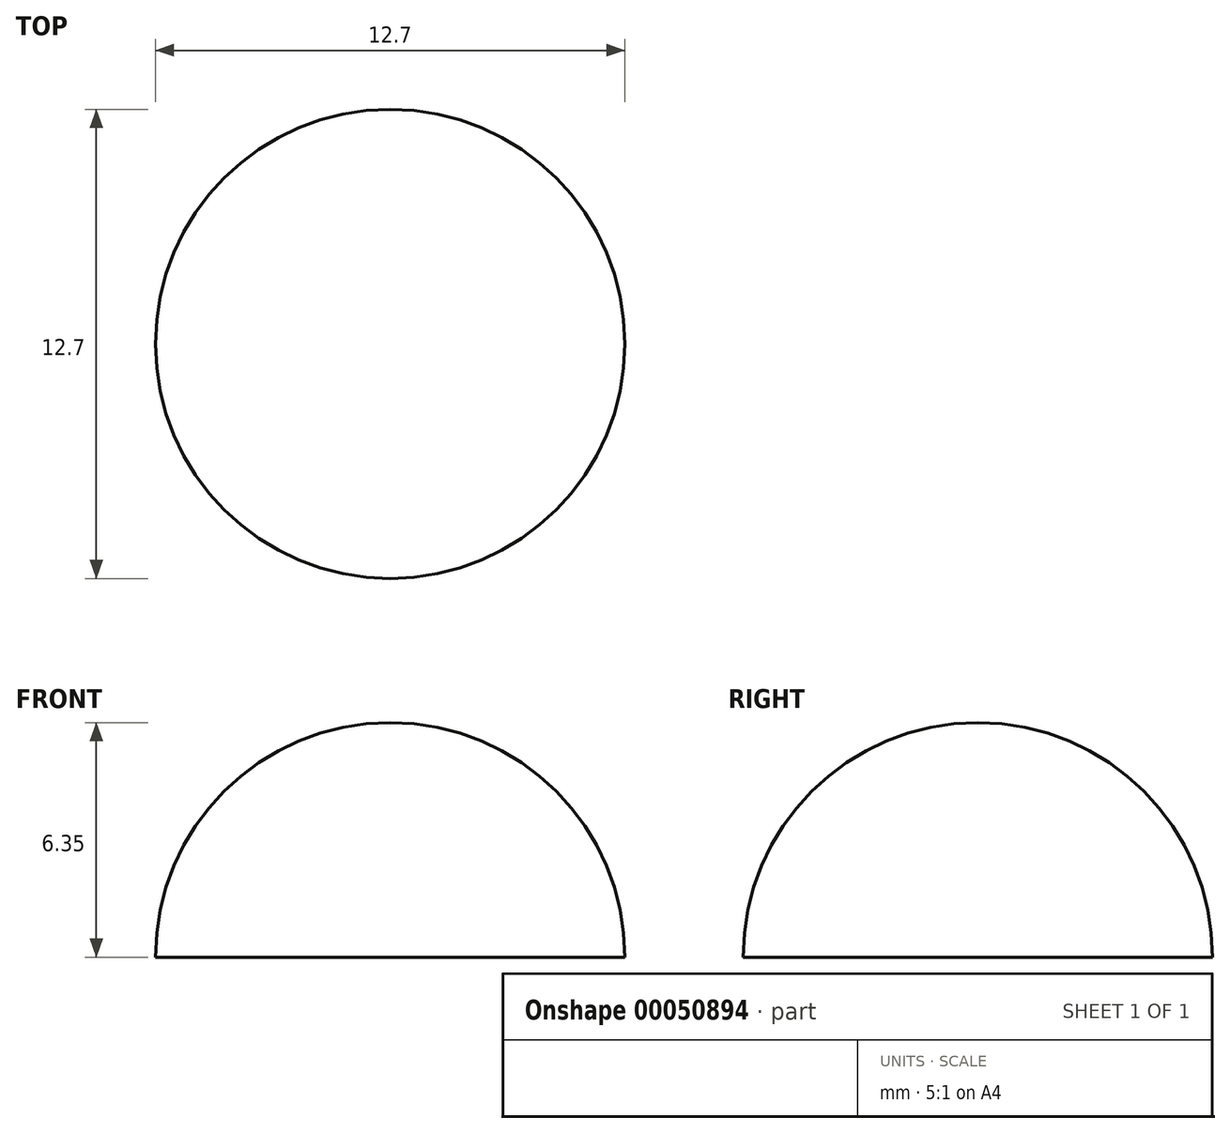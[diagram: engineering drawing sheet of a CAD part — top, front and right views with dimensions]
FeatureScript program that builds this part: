
annotation { "Feature Type Name" : "Feature", "Feature Type Description" : "" }
export const myFeature = defineFeature(function(context is Context, id is Id, definition is map)
    precondition{}
    {
        {
            var Q0;
            Q0=qCreatedBy(makeId("Top.planeOp"),FACE);
            var sketch = newSketch(context, id + "F0", { "sketchPlane" : qUnion([Q0])});
            skLineSegment(sketch, "E0", {"start": v(0, 0) * mm, "end": v(0, 6.35) * mm});
            skLineSegment(sketch, "E1.MirrorCS", {"start": v(0, 0) * mm, "end": v(0, -6.35) * mm});
            skArc(sketch, "E2", {"start": v(0, 6.35) * mm, "mid": v(-6.35, 0) * mm, "end": v(0, -6.35) * mm});
            skLineSegment(sketch, "E3", {"start": v(0, 6.35) * mm, "end": v(0, -6.35) * mm});
            skSolve(sketch);
        }
        {
            var Q0;
            {var subQ0=sQuery(id+"F0.wireOp",EDGE,"E2");Q0=makeQuery(id+"F0.imprint","IMPRINT",FACE,{"disambiguationData":[TD([[makeQuery(id+"F0.imprint","IMPRINT",EDGE,{"derivedFrom":subQ0}),1.0]])]});}
            var Q1;
            Q1=sQuery(id+"F0.wireOp",EDGE,"E3");
            revolve(context, id + "F1", {"entities" : qUnion([Q0]), "axis" : qUnion([Q1]), "revolveType" : RevolveType.ONE_DIRECTION, "oppositeDirection" : true, "angle" : 180 * degree});
        }
    });
